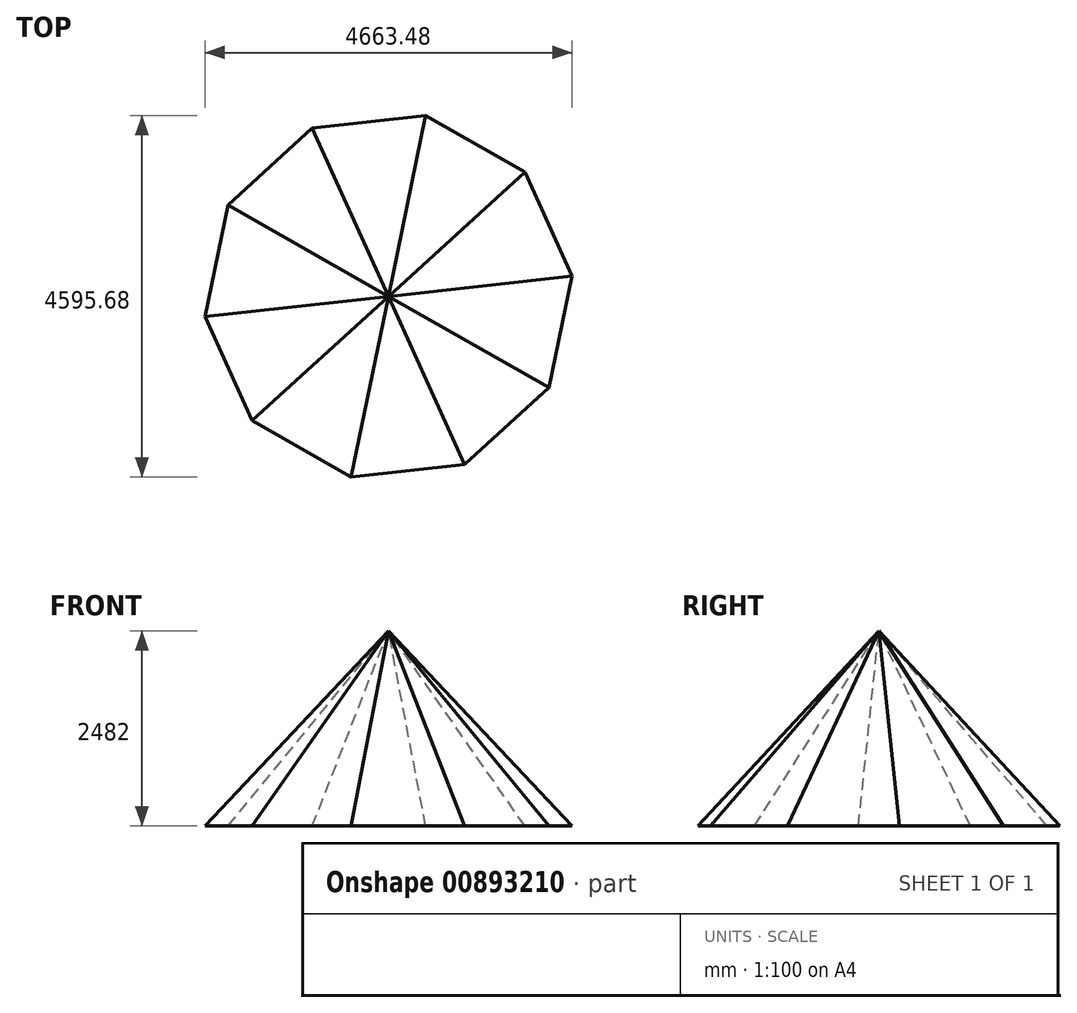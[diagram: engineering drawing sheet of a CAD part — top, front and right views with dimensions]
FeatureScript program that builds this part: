
annotation { "Feature Type Name" : "Feature", "Feature Type Description" : "" }
export const myFeature = defineFeature(function(context is Context, id is Id, definition is map)
    precondition{}
    {
        {
            var Q0;
            Q0=qCreatedBy(makeId("Front.planeOp"),FACE);
            var sketch = newSketch(context, id + "F0", { "sketchPlane" : qUnion([Q0])});
            skLineSegment(sketch, "E0", {"start": v(0, 0) * mm, "end": v(0, 2482) * mm});
            skSolve(sketch);
        }
        {
            var Q0;
            Q0=qCreatedBy(makeId("Top.planeOp"),FACE);
            var sketch = newSketch(context, id + "F1", { "sketchPlane" : qUnion([Q0])});
            skCircle(sketch, "E1.cCircle", {"center": v(0, 0) * mm, "radius": 2231.32 * mm, "construction": true});
            skLineSegment(sketch, "E1.0", {"start": v(-2331.74, -259.6) * mm, "end": v(-2039, 1160.54) * mm});
            skLineSegment(sketch, "E1.1", {"start": v(-2039, 1160.54) * mm, "end": v(-967.44, 2137.4) * mm});
            skLineSegment(sketch, "E1.2", {"start": v(-967.44, 2137.4) * mm, "end": v(473.65, 2297.84) * mm});
            skLineSegment(sketch, "E1.3", {"start": v(473.65, 2297.84) * mm, "end": v(1733.83, 1580.59) * mm});
            skLineSegment(sketch, "E1.4", {"start": v(1733.83, 1580.59) * mm, "end": v(2331.74, 259.6) * mm});
            skLineSegment(sketch, "E1.5", {"start": v(2331.74, 259.6) * mm, "end": v(2039, -1160.54) * mm});
            skLineSegment(sketch, "E1.6", {"start": v(2039, -1160.54) * mm, "end": v(967.44, -2137.4) * mm});
            skLineSegment(sketch, "E1.7", {"start": v(967.44, -2137.4) * mm, "end": v(-473.65, -2297.84) * mm});
            skLineSegment(sketch, "E1.8", {"start": v(-473.65, -2297.84) * mm, "end": v(-1733.83, -1580.59) * mm});
            skLineSegment(sketch, "E1.9", {"start": v(-1733.83, -1580.59) * mm, "end": v(-2331.74, -259.6) * mm});
            skPoint(sketch, "E1.0.midPoint", {"position": v(-2185.38, 450.47) * mm});
            skSolve(sketch);
        }
        {
            var Q0;
            Q0=makeQuery(id+"F1.imprint","IMPRINT",FACE,{"disambiguationData":[TD([[makeQuery(id+"F1.imprint","IMPRINT",EDGE,{"derivedFrom":sQuery(id+"F1.wireOp",EDGE,"E1.0")}),-1.0]])]});
            var Q1;
            Q1=sQuery(id+"F1.wireOp",EDGE,"E1.7");
            var Q2;
            Q2=sQuery(id+"F0.wireOp",VERTEX,"E0.end");
            loft(context, id + "F2", {"bodyType" : ToolBodyType.SURFACE, "sheetProfilesArray" : [{ "sheetProfileEntities" : qUnion([Q0]) }], "wireProfilesArray" : [{ "wireProfileEntities" : qUnion([Q1]) }, { "wireProfileEntities" : qUnion([Q2]) }]});
        }
        {
            var Q0;
            Q0=makeQuery(id+"F1.imprint","IMPRINT",FACE,{"disambiguationData":[TD([[makeQuery(id+"F1.imprint","IMPRINT",EDGE,{"derivedFrom":sQuery(id+"F1.wireOp",EDGE,"E1.0")}),-1.0]])]});
            var Q1;
            Q1=sQuery(id+"F0.wireOp",VERTEX,"E0.end");
            loft(context, id + "F3", {"sheetProfilesArray" : [{ "sheetProfileEntities" : qUnion([Q0]) }, { "sheetProfileEntities" : qUnion([Q1]) }]});
        }
    });
